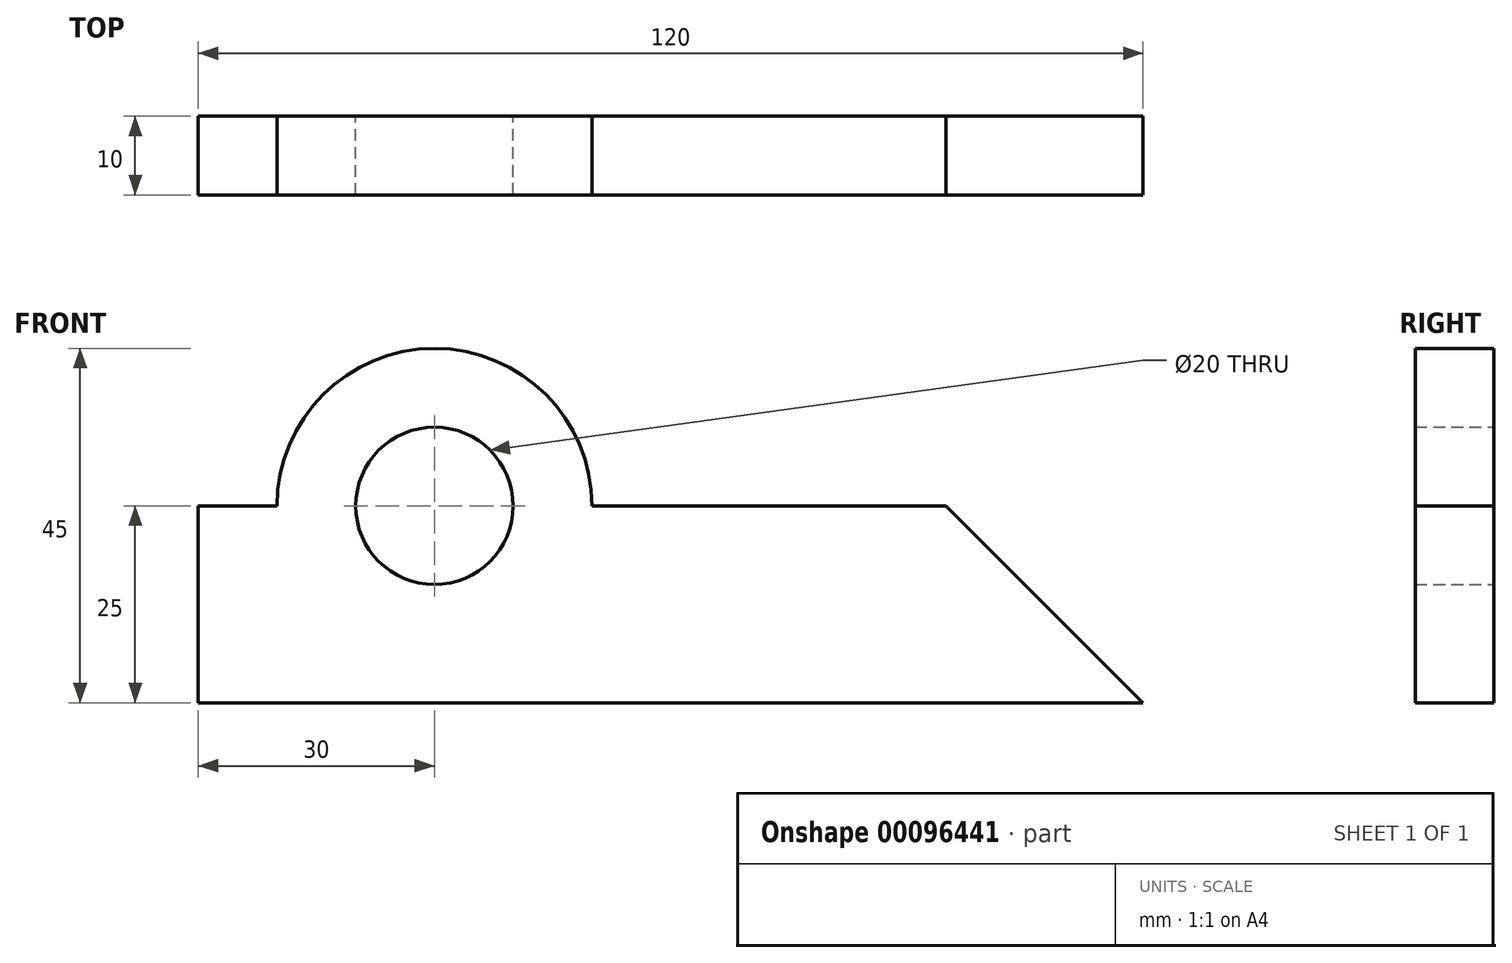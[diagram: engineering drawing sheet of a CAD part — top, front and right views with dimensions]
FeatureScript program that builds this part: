
annotation { "Feature Type Name" : "Feature", "Feature Type Description" : "" }
export const myFeature = defineFeature(function(context is Context, id is Id, definition is map)
    precondition{}
    {
        {
            var Q0;
            Q0=qCreatedBy(makeId("Front.planeOp"),FACE);
            var sketch = newSketch(context, id + "F0", { "sketchPlane" : qUnion([Q0])});
            skLineSegment(sketch, "E0", {"start": v(0, 0) * mm, "end": v(120, 0) * mm});
            skLineSegment(sketch, "E1", {"start": v(120, 0) * mm, "end": v(95, 25) * mm});
            skLineSegment(sketch, "E2", {"start": v(95, 25) * mm, "end": v(50, 25) * mm});
            skLineSegment(sketch, "E3", {"start": v(10, 25) * mm, "end": v(0, 25) * mm});
            skLineSegment(sketch, "E4", {"start": v(0, 25) * mm, "end": v(0, 0) * mm});
            skArc(sketch, "E5", {"start": v(50, 25) * mm, "mid": v(30, 45) * mm, "end": v(10, 25) * mm});
            skCircle(sketch, "E6", {"center": v(30, 25) * mm, "radius": 10 * mm});
            skLineSegment(sketch, "E7", {"start": v(10, 25) * mm, "end": v(50, 25) * mm, "construction": true});
            skSolve(sketch);
        }
        {
            var Q0;
            Q0 = qSketchRegion(id + "F0", true);
            extrude(context, id + "F1", {"entities" : qUnion([Q0]), "depth" : 10 * mm});
        }
    });
